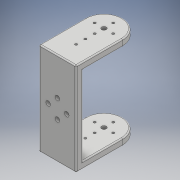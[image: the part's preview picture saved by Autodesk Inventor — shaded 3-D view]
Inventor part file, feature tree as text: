
AUTODESK INVENTOR PART (.ipt)
format: ipt  version: 2018 (Build 220112000, 112)  size: 243,200 bytes
history: native  units: mm
features: extrude x4, sketch x4, fillet x2
ambient origin geometry x8: Origin, YZ Plane, XZ Plane, XY Plane, X Axis, Y Axis, Z Axis, Center Point
bodies: Body1 (feature_tree)
feature tree (10):
  extrude  "Extrusion6"  Depth=40.0mm
  extrude  "Extrusion7"  Depth=2.0mm
  fillet  "Fillet3"  Radius=2.0mm
  sketch  "Sketch13"  dims[d50=2.0mm d51=8.0mm]
  extrude  "Extrusion8"  Depth=8.0mm
  extrude  "Extrusion9"  Depth=8.0mm
  fillet  "Fillet4"  Radius=24.0mm
  sketch  "Sketch11"  dims[d45=16.0mm d46=40.0mm]
  sketch  "Sketch12"  dims[d47=2.0mm d48=2.0mm d49=2.0mm]
  sketch  "Sketch14"  dims[d52=24.0mm d53=8.0mm d54=24.0mm d55=12.0mm d56=20.0mm d57=20.0mm d58=4.0mm d59=3.0mm d60=0.0mm d61=3.0mm d62=3.0mm d63=25.0mm d64=0.0mm d65=8.0mm d66=2.0mm d67=1.0mm d68=20.0mm d69=8.0mm d70=8.0mm d71=16.0mm d72=1.0mm d73=1.0mm d74=1.0mm d75=1.0mm d76=1.0mm d77=4.0mm d78=8.0mm d79=4.0mm d80=20.0mm d81=4.0mm d82=20.0mm d83=8.0mm d84=8.0mm d85=8.0mm d86=12.0mm d87=2.0mm d88=1.0mm d89=1.0mm d90=1.0mm d91=1.0mm d92=1.0mm d93=1.0mm d94=8.0mm d95=20.0mm d96=20.0mm d97=4.0mm d98=4.0mm d99=8.0mm d100=4.0mm d101=20.0mm d102=4.0mm d103=8.0mm d104=8.0mm d105=8.0mm d106=12.0mm d107=8.0mm d108=3.0mm d109=0.0mm d110=3.0mm d111=0.0mm d112=0.5mm]
